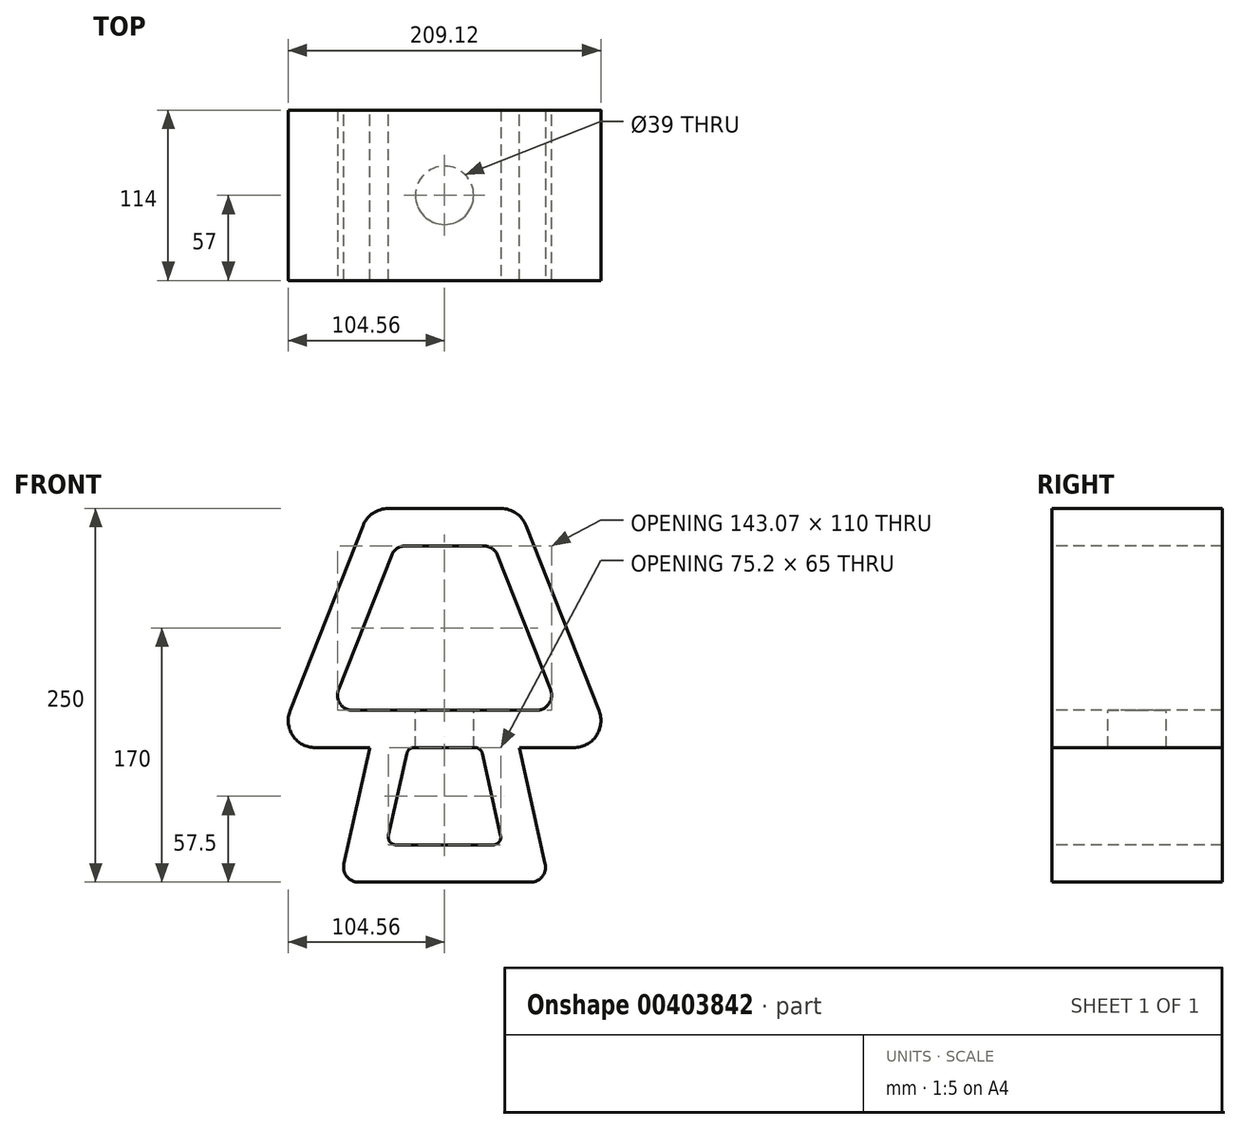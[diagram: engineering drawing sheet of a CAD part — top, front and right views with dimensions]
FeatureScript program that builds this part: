
annotation { "Feature Type Name" : "Feature", "Feature Type Description" : "" }
export const myFeature = defineFeature(function(context is Context, id is Id, definition is map)
    precondition{}
    {
        {
            var Q0;
            Q0=qCreatedBy(makeId("Front.planeOp"),FACE);
            var sketch = newSketch(context, id + "F0", { "sketchPlane" : qUnion([Q0])});
            skLineSegment(sketch, "E0", {"start": v(70, 0) * mm, "end": v(50, 90) * mm});
            skLineSegment(sketch, "E1", {"start": v(50, 90) * mm, "end": v(113, 90) * mm});
            skLineSegment(sketch, "E2", {"start": v(113, 90) * mm, "end": v(50, 250) * mm});
            skLineSegment(sketch, "E3.MirrorCS", {"start": v(-113, 90) * mm, "end": v(-50, 250) * mm});
            skLineSegment(sketch, "E4.MirrorCS", {"start": v(-70, 0) * mm, "end": v(-50, 90) * mm});
            skLineSegment(sketch, "E5.MirrorCS", {"start": v(-50, 90) * mm, "end": v(-113, 90) * mm});
            skLineSegment(sketch, "E6", {"start": v(50, 250) * mm, "end": v(-50, 250) * mm});
            skLineSegment(sketch, "E7", {"start": v(70, 0) * mm, "end": v(-70, 0) * mm});
            skSolve(sketch);
        }
        {
            var Q0;
            Q0=makeQuery(id+"F0.imprint","IMPRINT",FACE,{"disambiguationData":[TD([[makeQuery(id+"F0.imprint","IMPRINT",EDGE,{"derivedFrom":sQuery(id+"F0.wireOp",EDGE,"E0")}),1.0]])]});
            extrude(context, id + "F1", {"entities" : qUnion([Q0]), "endBound" : BoundingType.SYMMETRIC, "depth" : 114 * mm});
        }
        {
            var Q0;
            Q0=makeQuery(id+"F1.opExtrude","SWEPT_EDGE",EDGE,{"disambiguationData":[OSD([sQuery(id+"F0.wireOp",EDGE,"E2"),sQuery(id+"F0.wireOp",EDGE,"E6")])]});
            var Q1;
            Q1=makeQuery(id+"F1.opExtrude","SWEPT_EDGE",EDGE,{"disambiguationData":[OSD([sQuery(id+"F0.wireOp",EDGE,"E3.MirrorCS"),sQuery(id+"F0.wireOp",EDGE,"E6")])]});
            var Q2;
            Q2=makeQuery(id+"F1.opExtrude","SWEPT_EDGE",EDGE,{"disambiguationData":[OSD([sQuery(id+"F0.wireOp",EDGE,"E1"),sQuery(id+"F0.wireOp",EDGE,"E2")])]});
            var Q3;
            Q3=makeQuery(id+"F1.opExtrude","SWEPT_EDGE",EDGE,{"disambiguationData":[OSD([sQuery(id+"F0.wireOp",EDGE,"E3.MirrorCS"),sQuery(id+"F0.wireOp",EDGE,"E5.MirrorCS")])]});
            fillet(context, id + "F2", {"entities" : qUnion([Q0, Q1, Q2, Q3]), "radius" : 18 * mm, "tangentPropagation" : true, "allowEdgeOverflow" : false});
        }
        {
            var Q0;
            Q0=makeQuery(id+"F1.opExtrude","SWEPT_EDGE",EDGE,{"disambiguationData":[OSD([sQuery(id+"F0.wireOp",EDGE,"E0"),sQuery(id+"F0.wireOp",EDGE,"E7")])]});
            var Q1;
            Q1=makeQuery(id+"F1.opExtrude","SWEPT_EDGE",EDGE,{"disambiguationData":[OSD([sQuery(id+"F0.wireOp",EDGE,"E4.MirrorCS"),sQuery(id+"F0.wireOp",EDGE,"E7")])]});
            fillet(context, id + "F3", {"entities" : qUnion([Q0, Q1]), "radius" : 10 * mm, "tangentPropagation" : true, "allowEdgeOverflow" : false});
        }
        {
            var Q0;
            Q0=makeQuery(id+"F1.opExtrude","CAP_FACE",FACE,{"disambiguationData":[OSD([sQuery(id+"F0.wireOp",EDGE,"E0"),sQuery(id+"F0.wireOp",EDGE,"E1"),sQuery(id+"F0.wireOp",EDGE,"E2"),sQuery(id+"F0.wireOp",EDGE,"E3.MirrorCS"),sQuery(id+"F0.wireOp",EDGE,"E4.MirrorCS"),sQuery(id+"F0.wireOp",EDGE,"E5.MirrorCS"),sQuery(id+"F0.wireOp",EDGE,"E6"),sQuery(id+"F0.wireOp",EDGE,"E7")])],"isStart":false});
            var sketch = newSketch(context, id + "F4", { "sketchPlane" : qUnion([Q0])});
            skLineSegment(sketch, "E8", {"start": v(38.83, 25) * mm, "end": v(24.4, 90) * mm});
            skLineSegment(sketch, "E9.MirrorCS", {"start": v(-38.83, 25) * mm, "end": v(-24.4, 90) * mm});
            skLineSegment(sketch, "E10", {"start": v(38.83, 25) * mm, "end": v(-38.83, 25) * mm});
            skLineSegment(sketch, "E11", {"start": v(-24.4, 90) * mm, "end": v(24.4, 90) * mm});
            skSolve(sketch);
        }
        {
            var Q0;
            Q0=makeQuery(id+"F4.imprint","IMPRINT",FACE,{"disambiguationData":[TD([[makeQuery(id+"F4.imprint","IMPRINT",EDGE,{"derivedFrom":sQuery(id+"F4.wireOp",EDGE,"E8")}),1.0]])]});
            extrude(context, id + "F5", {"entities" : qUnion([Q0]), "operationType" : NewBodyOperationType.REMOVE, "endBound" : BoundingType.UP_TO_NEXT, "oppositeDirection" : true, "depth" : 25 * mm});
        }
        {
            var Q0;
            Q0=makeQuery(id+"F5.boolean.opBoolean","COPY",EDGE,{"derivedFrom":makeQuery(id+"F5.opExtrude","SWEPT_EDGE",EDGE,{"disambiguationData":[OSD([sQuery(id+"F4.wireOp",EDGE,"E9.MirrorCS"),sQuery(id+"F4.wireOp",EDGE,"E10")])]})});
            var Q1;
            Q1=makeQuery(id+"F5.boolean.opBoolean","COPY",EDGE,{"derivedFrom":makeQuery(id+"F5.opExtrude","SWEPT_EDGE",EDGE,{"disambiguationData":[OSD([sQuery(id+"F4.wireOp",EDGE,"E8"),sQuery(id+"F4.wireOp",EDGE,"E10")])]})});
            var Q2;
            Q2=makeQuery(id+"F5.boolean.opBoolean","COPY",EDGE,{"derivedFrom":makeQuery(id+"F5.opExtrude","SWEPT_EDGE",EDGE,{"disambiguationData":[OSD([sQuery(id+"F4.wireOp",EDGE,"E9.MirrorCS"),sQuery(id+"F4.wireOp",EDGE,"E11")])]})});
            var Q3;
            Q3=makeQuery(id+"F5.boolean.opBoolean","COPY",EDGE,{"derivedFrom":makeQuery(id+"F5.opExtrude","SWEPT_EDGE",EDGE,{"disambiguationData":[OSD([sQuery(id+"F4.wireOp",EDGE,"E8"),sQuery(id+"F4.wireOp",EDGE,"E11")])]})});
            fillet(context, id + "F6", {"entities" : qUnion([Q0, Q1, Q2, Q3]), "radius" : 5 * mm, "tangentPropagation" : true, "allowEdgeOverflow" : false});
        }
        {
            var Q0;
            Q0=makeQuery(id+"F1.opExtrude","CAP_FACE",FACE,{"disambiguationData":[OSD([sQuery(id+"F0.wireOp",EDGE,"E0"),sQuery(id+"F0.wireOp",EDGE,"E1"),sQuery(id+"F0.wireOp",EDGE,"E2"),sQuery(id+"F0.wireOp",EDGE,"E3.MirrorCS"),sQuery(id+"F0.wireOp",EDGE,"E4.MirrorCS"),sQuery(id+"F0.wireOp",EDGE,"E5.MirrorCS"),sQuery(id+"F0.wireOp",EDGE,"E6"),sQuery(id+"F0.wireOp",EDGE,"E7")])],"isStart":false});
            var sketch = newSketch(context, id + "F7", { "sketchPlane" : qUnion([Q0])});
            skLineSegment(sketch, "E12", {"start": v(76.28, 115) * mm, "end": v(32.97, 225) * mm});
            skLineSegment(sketch, "E13.MirrorCS", {"start": v(-76.28, 115) * mm, "end": v(-32.97, 225) * mm});
            skLineSegment(sketch, "E14", {"start": v(32.97, 225) * mm, "end": v(-32.97, 225) * mm});
            skLineSegment(sketch, "E15", {"start": v(-76.28, 115) * mm, "end": v(76.28, 115) * mm});
            skSolve(sketch);
        }
        {
            var Q0;
            Q0=makeQuery(id+"F7.imprint","IMPRINT",FACE,{"disambiguationData":[TD([[makeQuery(id+"F7.imprint","IMPRINT",EDGE,{"derivedFrom":sQuery(id+"F7.wireOp",EDGE,"E12")}),1.0]])]});
            extrude(context, id + "F8", {"entities" : qUnion([Q0]), "operationType" : NewBodyOperationType.REMOVE, "endBound" : BoundingType.UP_TO_NEXT, "oppositeDirection" : true, "depth" : 25 * mm});
        }
        {
            var Q0;
            Q0=makeQuery(id+"F8.boolean.opBoolean","COPY",EDGE,{"derivedFrom":makeQuery(id+"F8.opExtrude","SWEPT_EDGE",EDGE,{"disambiguationData":[OSD([sQuery(id+"F7.wireOp",EDGE,"E13.MirrorCS"),sQuery(id+"F7.wireOp",EDGE,"E15")])]})});
            var Q1;
            Q1=makeQuery(id+"F8.boolean.opBoolean","COPY",EDGE,{"derivedFrom":makeQuery(id+"F8.opExtrude","SWEPT_EDGE",EDGE,{"disambiguationData":[OSD([sQuery(id+"F7.wireOp",EDGE,"E12"),sQuery(id+"F7.wireOp",EDGE,"E15")])]})});
            var Q2;
            Q2=makeQuery(id+"F8.boolean.opBoolean","COPY",EDGE,{"derivedFrom":makeQuery(id+"F8.opExtrude","SWEPT_EDGE",EDGE,{"disambiguationData":[OSD([sQuery(id+"F7.wireOp",EDGE,"E12"),sQuery(id+"F7.wireOp",EDGE,"E14")])]})});
            var Q3;
            Q3=makeQuery(id+"F8.boolean.opBoolean","COPY",EDGE,{"derivedFrom":makeQuery(id+"F8.opExtrude","SWEPT_EDGE",EDGE,{"disambiguationData":[OSD([sQuery(id+"F7.wireOp",EDGE,"E13.MirrorCS"),sQuery(id+"F7.wireOp",EDGE,"E14")])]})});
            fillet(context, id + "F9", {"entities" : qUnion([Q0, Q1, Q2, Q3]), "radius" : 10 * mm, "tangentPropagation" : true, "allowEdgeOverflow" : false});
        }
        {
            var Q0;
            Q0=makeQuery(id+"F8.boolean.opBoolean","COPY",FACE,{"derivedFrom":makeQuery(id+"F8.opExtrude","SWEPT_FACE",FACE,{"disambiguationData":[OSD([sQuery(id+"F7.wireOp",EDGE,"E15")])]})});
            var sketch = newSketch(context, id + "F10", { "sketchPlane" : qUnion([Q0])});
            skCircle(sketch, "E16", {"center": v(0, 0) * mm, "radius": 19.5 * mm});
            skSolve(sketch);
        }
        {
            var Q0;
            Q0=makeQuery(id+"F10.imprint","IMPRINT",FACE,{"disambiguationData":[TD([[makeQuery(id+"F10.imprint","IMPRINT",EDGE,{"derivedFrom":sQuery(id+"F10.wireOp",EDGE,"E16")}),1.0]])]});
            extrude(context, id + "F11", {"entities" : qUnion([Q0]), "operationType" : NewBodyOperationType.REMOVE, "endBound" : BoundingType.UP_TO_NEXT, "oppositeDirection" : true, "depth" : 25 * mm});
        }
    });
